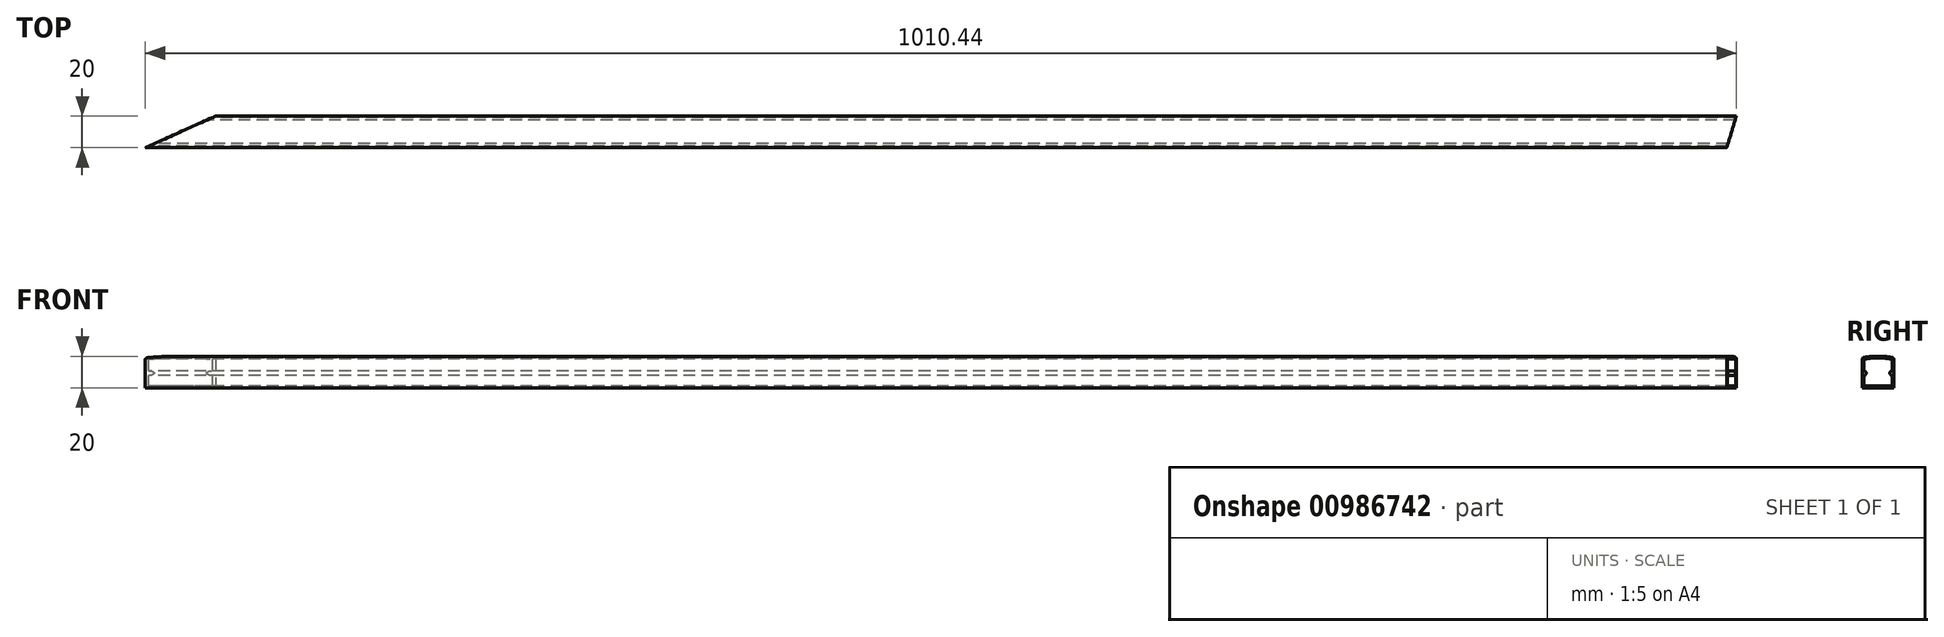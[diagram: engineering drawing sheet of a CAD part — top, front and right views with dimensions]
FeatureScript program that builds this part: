
annotation { "Feature Type Name" : "Feature", "Feature Type Description" : "" }
export const myFeature = defineFeature(function(context is Context, id is Id, definition is map)
    precondition{}
    {
        {
            var Q0;
            Q0=qCreatedBy(makeId("Right.planeOp"),FACE);
            var sketch = newSketch(context, id + "F0", { "sketchPlane" : qUnion([Q0])});
            skLineSegment(sketch, "E0.bottom", {"start": v(-10, -10) * mm, "end": v(10, -10) * mm});
            skLineSegment(sketch, "E0.top", {"start": v(-10, 10) * mm, "end": v(10, 10) * mm});
            skLineSegment(sketch, "E0.left", {"start": v(-10, -10) * mm, "end": v(-10, 10) * mm});
            skLineSegment(sketch, "E0.right", {"start": v(10, -10) * mm, "end": v(10, 10) * mm});
            skPoint(sketch, "E0.middle", {"position": v(0, 0) * mm});
            skSolve(sketch);
        }
        {
            var Q0;
            Q0=qCreatedBy(makeId("Right.planeOp"),FACE);
            var sketch = newSketch(context, id + "F1", { "sketchPlane" : qUnion([Q0])});
            skLineSegment(sketch, "E1.0", {"start": v(0, -10) * mm, "end": v(10, -10) * mm});
            skLineSegment(sketch, "E1.3", {"start": v(10, -10) * mm, "end": v(10, -0.2) * mm});
            skPoint(sketch, "E1.4", {"position": v(0, 0) * mm});
            skLineSegment(sketch, "E2.0", {"start": v(9, -9) * mm, "end": v(9, -2.2) * mm});
            skLineSegment(sketch, "E2.1", {"start": v(0, -9) * mm, "end": v(9, -9) * mm});
            skLineSegment(sketch, "E3", {"start": v(10, -0.2) * mm, "end": v(9, -0.2) * mm});
            skArc(sketch, "E4", {"start": v(9, -0.2) * mm, "mid": v(8.5, -0.7) * mm, "end": v(9, -1.2) * mm});
            skArc(sketch, "E5", {"start": v(9, -2.2) * mm, "mid": v(9.5, -1.7) * mm, "end": v(9, -1.2) * mm});
            skLineSegment(sketch, "E6", {"start": v(0, -9) * mm, "end": v(0, -10) * mm});
            skPoint(sketch, "E1.1.end.orphan", {"position": v(10, 10) * mm});
            skPoint(sketch, "E1.1.start.orphan", {"position": v(-10, 10) * mm});
            skPoint(sketch, "E1.2.end.orphan", {"position": v(-10, 10) * mm});
            skPoint(sketch, "E1.2.start.orphan", {"position": v(-10, -10) * mm});
            skPoint(sketch, "E7.orphan", {"position": v(-9, -9) * mm});
            skSolve(sketch);
        }
        {
            var Q0;
            Q0=qSketchRegion(id+"F1",true);
            extrude(context, id + "F2", {"entities" : qUnion([Q0]), "depth" : 1200 * mm, "offsetDistance" : 25 * mm});
        }
        {
            var Q0;
            Q0=qCreatedBy(makeId("Right.planeOp"),FACE);
            var sketch = newSketch(context, id + "F3", { "sketchPlane" : qUnion([Q0])});
            skPoint(sketch, "E8.2", {"position": v(0, 0) * mm});
            skLineSegment(sketch, "E8.5", {"start": v(10, -0.2) * mm, "end": v(9, -0.2) * mm});
            skArc(sketch, "E8.6", {"start": v(9, -0.2) * mm, "mid": v(8.5, -0.7) * mm, "end": v(9, -1.2) * mm});
            skArc(sketch, "E8.7", {"start": v(9, -2.2) * mm, "mid": v(9.5, -1.7) * mm, "end": v(9, -1.2) * mm});
            skPoint(sketch, "E8.9", {"position": v(10, 10) * mm});
            skPoint(sketch, "E8.10", {"position": v(10, 10) * mm});
            skPoint(sketch, "E8.11", {"position": v(-10, 10) * mm});
            skPoint(sketch, "E8.12", {"position": v(-10, 10) * mm});
            skPoint(sketch, "E8.13", {"position": v(-10, -10) * mm});
            skPoint(sketch, "E8.14", {"position": v(-9, -9) * mm});
            skPoint(sketch, "E8.15", {"position": v(-10, -10) * mm});
            skPoint(sketch, "E8.1.end.orphan", {"position": v(10, -0.2) * mm});
            skPoint(sketch, "E8.1.start.orphan", {"position": v(10, -10) * mm});
            skPoint(sketch, "E8.3.end.orphan", {"position": v(9, -2.2) * mm});
            skPoint(sketch, "E8.3.start.orphan", {"position": v(9, -9) * mm});
            skPoint(sketch, "E8.4.end.orphan", {"position": v(9, -9) * mm});
            skPoint(sketch, "E8.4.start.orphan", {"position": v(0, -9) * mm});
            skPoint(sketch, "E8.0.end.orphan", {"position": v(10, -10) * mm});
            skPoint(sketch, "E8.0.start.orphan", {"position": v(0, -10) * mm});
            skPoint(sketch, "E8.8.end.orphan", {"position": v(0, -10) * mm});
            skPoint(sketch, "E8.8.start.orphan", {"position": v(0, -9) * mm});
            skLineSegment(sketch, "E9", {"start": v(10, -0.2) * mm, "end": v(10, 8.17) * mm});
            skArc(sketch, "E10", {"start": v(9.18, 9.15) * mm, "mid": v(4.61, 9.79) * mm, "end": v(0, 10) * mm});
            skLineSegment(sketch, "E11", {"start": v(0, 10) * mm, "end": v(-15.57, 10) * mm, "construction": true});
            skPoint(sketch, "E12.visualSharp", {"position": v(10, 8.99) * mm});
            skArc(sketch, "E12.filletArc", {"start": v(10, 8.17) * mm, "mid": v(9.77, 8.8) * mm, "end": v(9.18, 9.15) * mm});
            skArc(sketch, "E13.0", {"start": v(9, 8.17) * mm, "mid": v(4.52, 8.8) * mm, "end": v(0, 9) * mm});
            skLineSegment(sketch, "E13.1", {"start": v(9, 0.8) * mm, "end": v(9, 8.17) * mm});
            skArc(sketch, "E13.2", {"start": v(9, 0.8) * mm, "mid": v(7.5, -0.7) * mm, "end": v(9, -2.2) * mm});
            skLineSegment(sketch, "E14", {"start": v(0, 10) * mm, "end": v(0, 9) * mm});
            skSolve(sketch);
        }
        {
            var Q0;
            Q0=qSketchRegion(id+"F3",true);
            extrude(context, id + "F4", {"entities" : qUnion([Q0]), "depth" : 1200 * mm, "offsetDistance" : 25 * mm});
        }
        {
            var Q0;
            Q0=makeQuery(id+"F2.opExtrude","SWEPT_BODY",BODY,{"disambiguationData":[OSD([sQuery(id+"F1.wireOp",EDGE,"E1.0"),sQuery(id+"F1.wireOp",EDGE,"E1.3"),sQuery(id+"F1.wireOp",EDGE,"E2.0"),sQuery(id+"F1.wireOp",EDGE,"E2.1"),sQuery(id+"F1.wireOp",EDGE,"E3"),sQuery(id+"F1.wireOp",EDGE,"E4"),sQuery(id+"F1.wireOp",EDGE,"E5"),sQuery(id+"F1.wireOp",EDGE,"E6")])]});
            var Q1;
            Q1=qCreatedBy(makeId("Front.planeOp"),FACE);
            mirror(context, id + "F5", {"operationType" : NewBodyOperationType.ADD, "entities" : qUnion([Q0]), "mirrorPlane" : qUnion([Q1])});
        }
        {
            var Q0;
            Q0=makeQuery(id+"F4.opExtrude","SWEPT_BODY",BODY,{"disambiguationData":[OSD([sQuery(id+"F3.wireOp",EDGE,"E8.5"),sQuery(id+"F3.wireOp",EDGE,"E8.6"),sQuery(id+"F3.wireOp",EDGE,"E8.7"),sQuery(id+"F3.wireOp",EDGE,"E9"),sQuery(id+"F3.wireOp",EDGE,"E10"),sQuery(id+"F3.wireOp",EDGE,"E12.filletArc"),sQuery(id+"F3.wireOp",EDGE,"E13.0"),sQuery(id+"F3.wireOp",EDGE,"E13.1"),sQuery(id+"F3.wireOp",EDGE,"E13.2"),sQuery(id+"F3.wireOp",EDGE,"E14")])]});
            var Q1;
            Q1=qCreatedBy(makeId("Front.planeOp"),FACE);
            mirror(context, id + "F6", {"operationType" : NewBodyOperationType.ADD, "entities" : qUnion([Q0]), "mirrorPlane" : qUnion([Q1])});
        }
        {
            var Q0;
            Q0=qCreatedBy(makeId("Top.planeOp"),FACE);
            var sketch = newSketch(context, id + "F7", { "sketchPlane" : qUnion([Q0])});
            skLineSegment(sketch, "E15", {"start": v(0, 0) * mm, "end": v(0, -10) * mm});
            skLineSegment(sketch, "E16", {"start": v(0, -10) * mm, "end": v(44.5, 10) * mm});
            skLineSegment(sketch, "E17", {"start": v(44.5, 10) * mm, "end": v(0, 10) * mm});
            skLineSegment(sketch, "E18", {"start": v(0, 10) * mm, "end": v(0, 0) * mm});
            skLineSegment(sketch, "E19", {"start": v(1004.4, -10) * mm, "end": v(1010.44, 10) * mm});
            skLineSegment(sketch, "E20", {"start": v(1010.44, 10) * mm, "end": v(1208.1, 10) * mm});
            skLineSegment(sketch, "E21.bottom", {"start": v(1004.4, -10) * mm, "end": v(1208.1, -10) * mm});
            skLineSegment(sketch, "E21.top", {"start": v(1004.4, 10) * mm, "end": v(1208.1, 10) * mm});
            skLineSegment(sketch, "E21.right", {"start": v(1208.1, -10) * mm, "end": v(1208.1, 10) * mm});
            skLineSegment(sketch, "E22", {"start": v(1004.4, -10) * mm, "end": v(1004.4, 10) * mm, "construction": true});
            skSolve(sketch);
        }
        {
            var Q0;
            Q0=qSketchRegion(id+"F7",true);
            extrude(context, id + "F8", {"entities" : qUnion([Q0]), "operationType" : NewBodyOperationType.REMOVE, "endBound" : BoundingType.THROUGH_ALL, "depth" : 25 * mm, "offsetDistance" : 25 * mm, "hasSecondDirection" : true, "secondDirectionBound" : SecondDirectionBoundingType.THROUGH_ALL, "secondDirectionOppositeDirection" : true, "secondDirectionDepth" : 25 * mm});
        }
    });
